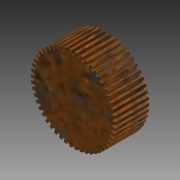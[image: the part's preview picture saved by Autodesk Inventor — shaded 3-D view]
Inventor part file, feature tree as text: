
AUTODESK INVENTOR PART (.ipt)
format: ipt  version: 2016 SP2 (Build 200236200, 236)  size: 393,216 bytes
history: native  units: mm
features: extrude x2, sketch x2
ambient origin geometry x8: Origin, YZ Plane, XZ Plane, XY Plane, X Axis, Y Axis, Z Axis, Center Point
bodies: Solid1 (feature_tree)
feature tree (4):
  extrude  "Extrusion1"  Depth=2.0mm TaperAngle=0.0deg
  extrude  "Extrusion2"  Depth=2.5mm
  sketch  "Sketch1"  dims[d0=5.0mm d1=2.0mm d2=0.0mm]
  sketch  "Sketch2"  dims[d4=0.05mm d9=2.3mm d10=1.745329mm d16=0.198554mm d25=2.5mm d26=500.0mm d28=360.0deg d30=6.5mm d31=0.0mm]
